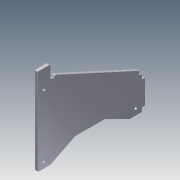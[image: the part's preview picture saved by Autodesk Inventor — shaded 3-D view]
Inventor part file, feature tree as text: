
AUTODESK INVENTOR PART (.ipt)
format: ipt  version: 2014 (Build 180170000, 170)  size: 159,232 bytes
history: native  units: mm
features: extrude x5, sketch x4, fillet x1
ambient origin geometry x8: Origin, YZ Plane, XZ Plane, XY Plane, X Axis, Y Axis, Z Axis, Center Point
bodies: Solid1 (feature_tree)
feature tree (10):
  extrude  "Extrusion1"  Depth=25.0mm
  extrude  "Extrusion2"  Depth=210.0mm
  extrude  "Extrusion3"  Depth=25.0mm
  extrude  "Extrusion4"  Depth=6.0mm
  extrude  "Extrusion5"  Depth=25.0mm
  fillet  "Fillet1"  Radius=3.0mm
  sketch  "Sketch2"  dims[d0=175.0mm d1=25.0mm]
  sketch  "Sketch3"  dims[d3=65.0mm d4=210.0mm]
  sketch  "Sketch4"  dims[d5=6.0mm d6=0.0mm d8=25.0mm]
  sketch  "Sketch6"  dims[d9=25.0mm d10=50.0mm d11=25.0mm d12=3.0mm d13=0.0mm d14=8.1mm d15=8.1mm d16=6.0mm d17=6.0mm d18=0.0mm d19=12.5mm d20=37.5mm d21=12.5mm d22=12.5mm d23=5.4mm d24=6.0mm d25=0.0mm d26=2.0mm d27=185.0mm d28=85.0mm d33=8.1mm d34=6.0mm d35=0.0mm d36=8.1mm d38=6.0mm]
